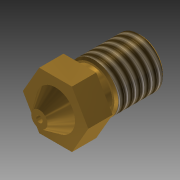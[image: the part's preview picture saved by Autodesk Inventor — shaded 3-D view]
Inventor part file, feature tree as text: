
AUTODESK INVENTOR PART (.ipt)
format: ipt  version: 2015 (Build 190159000, 159)  size: 152,576 bytes
history: native  units: mm
features: sketch x4, chamfer x2, hole x2, other x1, revolve x1, thread x1, extrude x1
ambient origin geometry x8: Origin, YZ Plane, XZ Plane, XY Plane, X Axis, Y Axis, Z Axis, Center Point
bodies: Body1 (feature_tree)
feature tree (12):
  other  "Твердое тело1"
  revolve  "Вращение1"
  chamfer  "Фаска1"  Distance=15.0mm
  thread  "Резьба1"
  sketch  "Эскиз2"
  sketch  "Эскиз3"
  hole  "Отверстие2"  [1 undecoded]
  chamfer  "Фаска2"  Distance=10.5mm
  hole  "Отверстие3"  [1 undecoded]
  extrude  "Выдавливание1"  Depth=6.0mm
  sketch  "Эскиз1"
  sketch  "Эскиз4"
note: 2 required parameter values undecoded (feature->parameter linkage not recoverable at this tier; creation-order binding heuristic only, values carry confidence <= 0.55)
